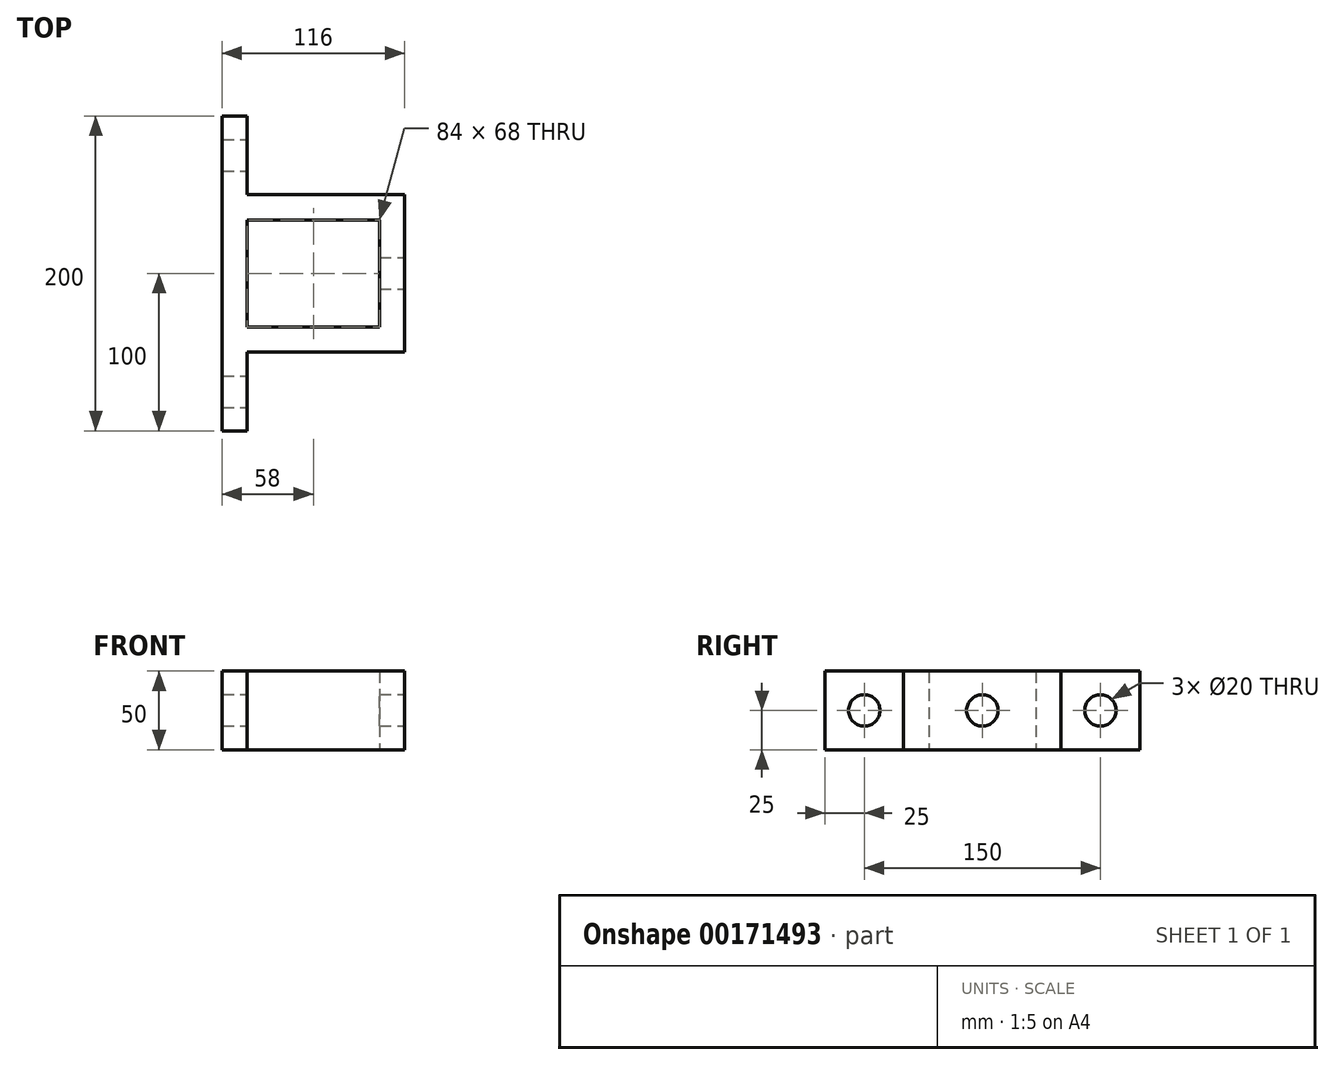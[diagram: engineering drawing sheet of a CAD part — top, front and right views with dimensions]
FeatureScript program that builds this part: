
annotation { "Feature Type Name" : "Feature", "Feature Type Description" : "" }
export const myFeature = defineFeature(function(context is Context, id is Id, definition is map)
    precondition{}
    {
        {
            var Q0;
            Q0=qCreatedBy(makeId("Top.planeOp"),FACE);
            var sketch = newSketch(context, id + "F0", { "sketchPlane" : qUnion([Q0])});
            skLineSegment(sketch, "E0", {"start": v(0, 0) * mm, "end": v(0, 200) * mm});
            skLineSegment(sketch, "E1", {"start": v(0, 200) * mm, "end": v(16, 200) * mm});
            skLineSegment(sketch, "E2", {"start": v(16, 200) * mm, "end": v(16, 150) * mm});
            skLineSegment(sketch, "E3", {"start": v(16, 150) * mm, "end": v(116, 150) * mm});
            skLineSegment(sketch, "E4", {"start": v(116, 150) * mm, "end": v(116, 50) * mm});
            skLineSegment(sketch, "E5", {"start": v(116, 50) * mm, "end": v(16, 50) * mm});
            skLineSegment(sketch, "E6", {"start": v(16, 50) * mm, "end": v(16, 0) * mm});
            skLineSegment(sketch, "E7", {"start": v(16, 0) * mm, "end": v(0, 0) * mm});
            skLineSegment(sketch, "E8.bottom", {"start": v(16, 134) * mm, "end": v(100, 134) * mm});
            skLineSegment(sketch, "E8.top", {"start": v(16, 66) * mm, "end": v(100, 66) * mm});
            skLineSegment(sketch, "E8.left", {"start": v(16, 134) * mm, "end": v(16, 66) * mm});
            skLineSegment(sketch, "E8.right", {"start": v(100, 134) * mm, "end": v(100, 66) * mm});
            skSolve(sketch);
        }
        {
            var Q0;
            Q0=makeQuery(id+"F0.imprint","IMPRINT",FACE,{"disambiguationData":[TD([[makeQuery(id+"F0.imprint","IMPRINT",EDGE,{"derivedFrom":sQuery(id+"F0.wireOp",EDGE,"E0")}),-1.0]])]});
            extrude(context, id + "F1", {"entities" : qUnion([Q0]), "depth" : 50 * mm});
        }
        {
            var Q0;
            Q0=makeQuery(id+"F1.opExtrude","SWEPT_FACE",FACE,{"disambiguationData":[OSD([sQuery(id+"F0.wireOp",EDGE,"E6")])]});
            var sketch = newSketch(context, id + "F2", { "sketchPlane" : qUnion([Q0])});
            skLineSegment(sketch, "E9", {"start": v(0, 25) * mm, "end": v(25, 25) * mm});
            skLineSegment(sketch, "E10", {"start": v(25, 25) * mm, "end": v(175, 25) * mm});
            skLineSegment(sketch, "E11", {"start": v(25, 0) * mm, "end": v(25, 25) * mm});
            skLineSegment(sketch, "E12.0", {"start": v(200, 50) * mm, "end": v(200, 0) * mm});
            skLineSegment(sketch, "E13", {"start": v(175, 25) * mm, "end": v(200, 25) * mm});
            skSolve(sketch);
        }
        {
            var Q0;
            Q0=makeQuery(id+"F1.opExtrude","SWEPT_FACE",FACE,{"disambiguationData":[OSD([sQuery(id+"F0.wireOp",EDGE,"E4")])]});
            var sketch = newSketch(context, id + "F3", { "sketchPlane" : qUnion([Q0])});
            skLineSegment(sketch, "E14", {"start": v(50, 25) * mm, "end": v(100, 25) * mm});
            skPoint(sketch, "E14.endSnap0", {"position": v(100, 0) * mm});
            skSolve(sketch);
        }
        {
            var Q0;
            Q0=sQuery(id+"F2.wireOp",VERTEX,"E11.end");
            var Q1;
            Q1=sQuery(id+"F2.wireOp",VERTEX,"E13.start");
            var Q2;
            Q2=makeQuery(id+"F1.opExtrude","SWEPT_BODY",BODY,{"disambiguationData":[OSD([sQuery(id+"F0.wireOp",EDGE,"E0"),sQuery(id+"F0.wireOp",EDGE,"E1"),sQuery(id+"F0.wireOp",EDGE,"E2"),sQuery(id+"F0.wireOp",EDGE,"E3"),sQuery(id+"F0.wireOp",EDGE,"E4"),sQuery(id+"F0.wireOp",EDGE,"E5"),sQuery(id+"F0.wireOp",EDGE,"E6"),sQuery(id+"F0.wireOp",EDGE,"E7"),sQuery(id+"F0.wireOp",EDGE,"E8.bottom"),sQuery(id+"F0.wireOp",EDGE,"E8.top"),sQuery(id+"F0.wireOp",EDGE,"E8.left"),sQuery(id+"F0.wireOp",EDGE,"E8.right")])]});
            hole(context, id + "F4", {"style" : HoleStyle.SIMPLE, "endStyle" : HoleEndStyle.THROUGH, "holeDiameter" : 20 * mm, "isTappedThrough" : true, "tappedDepth" : 12 * mm, "tapClearance" : 3, "locations" : qUnion([Q0, Q1]), "scope" : qUnion([Q2])});
        }
        {
            var Q0;
            Q0=sQuery(id+"F3.wireOp",VERTEX,"E14.end");
            var Q1;
            Q1=makeQuery(id+"F1.opExtrude","SWEPT_BODY",BODY,{"disambiguationData":[OSD([sQuery(id+"F0.wireOp",EDGE,"E0"),sQuery(id+"F0.wireOp",EDGE,"E1"),sQuery(id+"F0.wireOp",EDGE,"E2"),sQuery(id+"F0.wireOp",EDGE,"E3"),sQuery(id+"F0.wireOp",EDGE,"E4"),sQuery(id+"F0.wireOp",EDGE,"E5"),sQuery(id+"F0.wireOp",EDGE,"E6"),sQuery(id+"F0.wireOp",EDGE,"E7"),sQuery(id+"F0.wireOp",EDGE,"E8.bottom"),sQuery(id+"F0.wireOp",EDGE,"E8.top"),sQuery(id+"F0.wireOp",EDGE,"E8.left"),sQuery(id+"F0.wireOp",EDGE,"E8.right")])]});
            hole(context, id + "F5", {"style" : HoleStyle.SIMPLE, "endStyle" : HoleEndStyle.BLIND, "holeDiameter" : 20 * mm, "holeDepth" : 50 * mm, "isTappedThrough" : true, "tappedDepth" : 12 * mm, "tapClearance" : 3, "locations" : qUnion([Q0]), "scope" : qUnion([Q1])});
        }
    });
